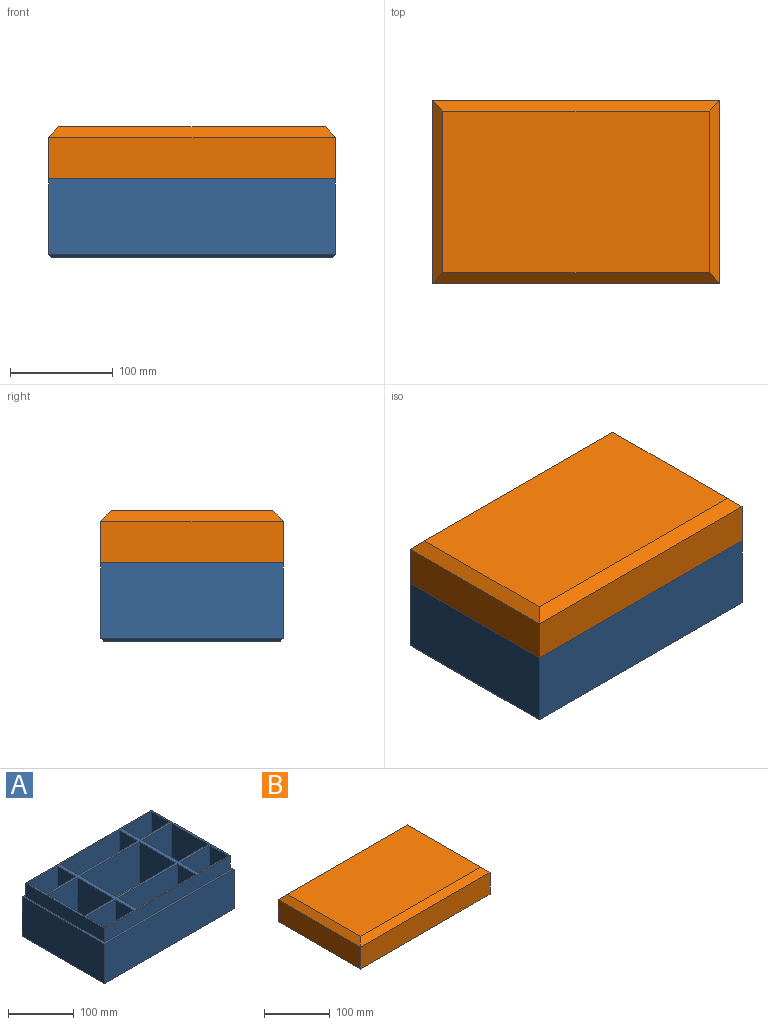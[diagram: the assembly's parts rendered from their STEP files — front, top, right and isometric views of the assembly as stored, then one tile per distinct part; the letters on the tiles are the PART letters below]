
ASSEMBLY  parts=2 mates=1
PART A: 60 faces, bbox 279.4x177.8x101.6 mm
  f0: plane 272.16x169.19mm, normal (0,0,1), area 6046.8mm2, adj f1,f2,f3,f4,f5,f6,f7,f8
  f1: plane 76.2x63.5mm, normal (0,-1,0), area 4838.7mm2, adj f0,f11,f20,f34
  f2: plane 127x76.2mm, normal (0,-1,0), area 9677.4mm2, adj f0,f10,f35,f37
  f3: plane 76.2x39.37mm, normal (1,0,0), area 3000mm2, adj f0,f15,f19,f23
  f4: plane 78.74x76.2mm, normal (1,0,0), area 6000mm2, adj f0,f16,f22,f44
  f5: plane 127x76.2mm, normal (0,1,0), area 9677.4mm2, adj f0,f14,f25,f27
  f6: plane 76.2x63.5mm, normal (0,1,0), area 4838.7mm2, adj f0,f7,f13,f28
  f7: plane 76.2x39.37mm, normal (-1,0,0), area 3000mm2, adj f0,f6,f13,f29
  f8: plane 78.74x76.2mm, normal (-1,0,0), area 6000mm2, adj f0,f12,f30,f32
  f9: plane 63.5x39.37mm, normal (0,0,1), area 2500mm2, adj f17,f18,f38,f39
  f10: plane 127x39.37mm, normal (0,0,1), area 5000mm2, adj f2,f35,f36,f37
  f11: plane 63.5x39.37mm, normal (0,0,1), area 2500mm2, adj f1,f20,f33,f34
  f12: plane 78.74x63.5mm, normal (0,0,1), area 5000mm2, adj f8,f30,f31,f32
  f13: plane 63.5x39.37mm, normal (0,0,1), area 2500mm2, adj f6,f7,f28,f29
  f14: plane 127x39.37mm, normal (0,0,1), area 5000mm2, adj f5,f25,f26,f27
  f15: plane 63.5x39.37mm, normal (0,0,1), area 2500mm2, adj f3,f19,f23,f24
  f16: plane 78.74x63.5mm, normal (0,0,1), area 5000mm2, adj f4,f21,f22,f44
  f17: plane 76.2x63.5mm, normal (0,-1,0), area 4838.7mm2, adj f0,f9,f18,f38
  f18: plane 76.2x39.37mm, normal (1,0,0), area 3000mm2, adj f0,f9,f17,f39
  f19: plane 76.2x63.5mm, normal (0,1,0), area 4838.7mm2, adj f0,f3,f15,f24
  f20: plane 76.2x39.37mm, normal (-1,0,0), area 3000mm2, adj f0,f1,f11,f33
  f21: plane 78.74x76.2mm, normal (-1,0,0), area 6000mm2, adj f0,f16,f22,f44
  f22: plane 76.2x63.5mm, normal (0,1,0), area 4838.7mm2, adj f0,f4,f16,f21
  f23: plane 76.2x63.5mm, normal (0,-1,0), area 4838.7mm2, adj f0,f3,f15,f24
  f24: plane 76.2x39.37mm, normal (-1,0,0), area 3000mm2, adj f0,f15,f19,f23
  f25: plane 76.2x39.37mm, normal (1,0,0), area 3000mm2, adj f0,f5,f14,f26
  f26: plane 127x76.2mm, normal (0,-1,0), area 9677.4mm2, adj f0,f14,f25,f27
  f27: plane 76.2x39.37mm, normal (-1,0,0), area 3000mm2, adj f0,f5,f14,f26
  f28: plane 76.2x39.37mm, normal (1,0,0), area 3000mm2, adj f0,f6,f13,f29
  f29: plane 76.2x63.5mm, normal (0,-1,0), area 4838.7mm2, adj f0,f7,f13,f28
  f30: plane 76.2x63.5mm, normal (0,1,0), area 4838.7mm2, adj f0,f8,f12,f31
  f31: plane 78.74x76.2mm, normal (1,0,0), area 6000mm2, adj f0,f12,f30,f32
  f32: plane 76.2x63.5mm, normal (0,-1,0), area 4838.7mm2, adj f0,f8,f12,f31
  f33: plane 76.2x63.5mm, normal (0,1,0), area 4838.7mm2, adj f0,f11,f20,f34
  f34: plane 76.2x39.37mm, normal (1,0,0), area 3000mm2, adj f0,f1,f11,f33
  f35: plane 76.2x39.37mm, normal (-1,0,0), area 3000mm2, adj f0,f2,f10,f36
  f36: plane 127x76.2mm, normal (0,1,0), area 9677.4mm2, adj f0,f10,f35,f37
  f37: plane 76.2x39.37mm, normal (1,0,0), area 3000mm2, adj f0,f2,f10,f36
  f38: plane 76.2x39.37mm, normal (-1,0,0), area 3000mm2, adj f0,f9,f17,f39
  f39: plane 76.2x63.5mm, normal (0,1,0), area 4838.7mm2, adj f0,f9,f18,f38
  f40: plane 127x76.2mm, normal (0,1,0), area 9677.4mm2, adj f0,f41,f43,f45
  f41: plane 78.74x76.2mm, normal (1,0,0), area 6000mm2, adj f0,f40,f42,f45
  f42: plane 127x76.2mm, normal (0,-1,0), area 9677.4mm2, adj f0,f41,f43,f45
  f43: plane 78.74x76.2mm, normal (-1,0,0), area 6000mm2, adj f0,f40,f42,f45
  f44: plane 76.2x63.5mm, normal (0,-1,0), area 4838.7mm2, adj f0,f4,f16,f21
  f45: plane 127x78.74mm, normal (0,0,1), area 10000mm2, adj f40,f41,f42,f43
  f46: plane 169.19x25.4mm, normal (-1,0,0), area 4297.4mm2, adj f0,f47,f49,f50
  f47: plane 272.16x25.4mm, normal (0,1,0), area 6912.9mm2, adj f0,f46,f48,f50
  f48: plane 169.19x25.4mm, normal (1,0,0), area 4297.4mm2, adj f0,f47,f49,f50
  f49: plane 272.16x25.4mm, normal (0,-1,0), area 6912.9mm2, adj f0,f46,f48,f50
  f50: plane 279.4x177.8mm, normal (0,0,1), area 3630.6mm2, adj f46,f47,f48,f49,f52,f53,f54,f55
  f51: plane 274.32x172.72mm, normal (0,0,-1), area 47380.6mm2, adj f56,f57,f58,f59
  f52: plane 177.8x73.66mm, normal (1,0,0), area 13096.7mm2, adj f50,f53,f55,f59
  f53: plane 279.4x73.66mm, normal (0,-1,0), area 20580.6mm2, adj f50,f52,f54,f58
  f54: plane 177.8x73.66mm, normal (-1,0,0), area 13096.7mm2, adj f50,f53,f55,f56
  f55: plane 279.4x73.66mm, normal (0,1,0), area 20580.6mm2, adj f50,f52,f54,f57
  f56: plane 177.8x2.54mm, normal (-0.71,0,-0.71), area 629.6mm2, adj f51,f54,f57,f58
  f57: plane 279.4x2.54mm, normal (0,0.71,-0.71), area 994.5mm2, adj f51,f55,f56,f59
  f58: plane 279.4x2.54mm, normal (0,-0.71,-0.71), area 994.5mm2, adj f51,f53,f56,f59
  f59: plane 177.8x2.54mm, normal (0.71,0,-0.71), area 629.6mm2, adj f51,f52,f57,f58
PART B: 24 faces, bbox 279.4x177.8x50.8 mm
  f0: plane 279.4x40.64mm, normal (0,1,0), area 11354.8mm2, adj f1,f3,f6,f9
  f1: plane 177.8x40.64mm, normal (-1,0,0), area 7225.8mm2, adj f0,f2,f8,f9
  f2: plane 279.4x40.64mm, normal (0,-1,0), area 11354.8mm2, adj f1,f3,f7,f9
  f3: plane 177.8x40.64mm, normal (1,0,0), area 7225.8mm2, adj f0,f2,f5,f9
  f4: plane 259.08x157.48mm, normal (0,0,1), area 40799.9mm2, adj f5,f6,f7,f8
  f5: plane 177.8x10.16mm, normal (0.71,0,0.71), area 2408.7mm2, adj f3,f4,f6,f7
  f6: plane 279.4x10.16mm, normal (0,0.71,0.71), area 3868.6mm2, adj f0,f4,f5,f8
  f7: plane 279.4x10.16mm, normal (0,-0.71,0.71), area 3868.6mm2, adj f2,f4,f5,f8
  f8: plane 177.8x10.16mm, normal (-0.71,0,0.71), area 2408.7mm2, adj f1,f4,f6,f7
  f9: plane 279.4x177.8mm, normal (0,0,-1), area 1362.7mm2, adj f0,f1,f2,f3,f20,f21,f22,f23
  f10: plane 273.69x170.71mm, normal (0,0,-1), area 2689.5mm2, adj f11,f12,f13,f14,f16,f17,f18,f19
  f11: plane 273.69x23.62mm, normal (0,1,0), area 6465mm2, adj f10,f12,f14,f22
  f12: plane 170.71x23.62mm, normal (1,0,0), area 4032.6mm2, adj f10,f11,f13,f23
  f13: plane 273.69x23.62mm, normal (0,-1,0), area 6465mm2, adj f10,f12,f14,f21
  f14: plane 170.71x23.62mm, normal (-1,0,0), area 4032.6mm2, adj f10,f11,f13,f20
  f15: plane 266.7x165.1mm, normal (0,0,-1), area 44032.2mm2, adj f16,f17,f18,f19
  f16: plane 266.7x10.16mm, normal (0,1,0), area 2709.7mm2, adj f10,f15,f17,f19
  f17: plane 165.1x10.16mm, normal (-1,0,0), area 1677.4mm2, adj f10,f15,f16,f18
  f18: plane 266.7x10.16mm, normal (0,-1,0), area 2709.7mm2, adj f10,f15,f17,f19
  f19: plane 165.1x10.16mm, normal (1,0,0), area 1677.4mm2, adj f10,f15,f16,f18
  f20: plane 174.27x1.78mm, normal (-0.71,0,-0.71), area 433.7mm2, adj f9,f14,f21,f22
  f21: plane 277.24x1.78mm, normal (0,-0.71,-0.71), area 692.6mm2, adj f9,f13,f20,f23
  f22: plane 277.24x1.78mm, normal (0,0.71,-0.71), area 692.6mm2, adj f9,f11,f20,f23
  f23: plane 174.27x1.78mm, normal (0.71,0,-0.71), area 433.7mm2, adj f9,f12,f21,f22
PLACE A at identity
PLACE B t=(0,0,101.6)mm
MATE fastened B.f2 <-> A.f53  axis (0,-1,0) through (-139.7,-88.9,76.2)mm
